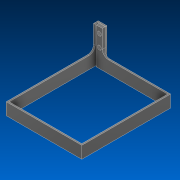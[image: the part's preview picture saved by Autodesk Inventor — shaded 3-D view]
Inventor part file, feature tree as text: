
AUTODESK INVENTOR PART (.ipt)
format: ipt  version: 2022.2 (Build 262287000, 287)  size: 163,328 bytes
history: native  units: in
note: dims shown in document units (in); Inventor stores cm internally (conversion verified against a paired STEP export)
features: sketch x3, extrude x2, hole x1, fillet x1, projected_geometry x1
ambient origin geometry x8: Origin, YZ Plane, XZ Plane, XY Plane, X Axis, Y Axis, Z Axis, Center Point
bodies: Solid1 (feature_tree)
feature tree (8):
  extrude  "Extrusion1"  Depth=7.1in
  extrude  "Extrusion4"  Depth=0.125in
  hole  "Hole2"  [1 undecoded]
  fillet  "Fillet3"  Radius=0.01in
  sketch  "Sketch1"  dims[d2=6.0in d3=7.1in]
  sketch  "Sketch5"  dims[d4=1.0in d5=0.0in d29=0.125in]
  projected_geometry  "Projected Loop2"
  sketch  "Sketch6"  dims[d30=0.125in d31=0.1in d32=0.01in d33=0.5in d34=2.0in d35=0.0in d36=0.5in d37=1.0in d38=0.25in d39=0.175in d40=0.75in d41=0.35in d42=0.1in d43=0.5635in d44=1.0in d45=0.8108in d46=0.5in d47=0.5in]
note: 1 required parameter value undecoded (feature->parameter linkage not recoverable at this tier; creation-order binding heuristic only, values carry confidence <= 0.55)
